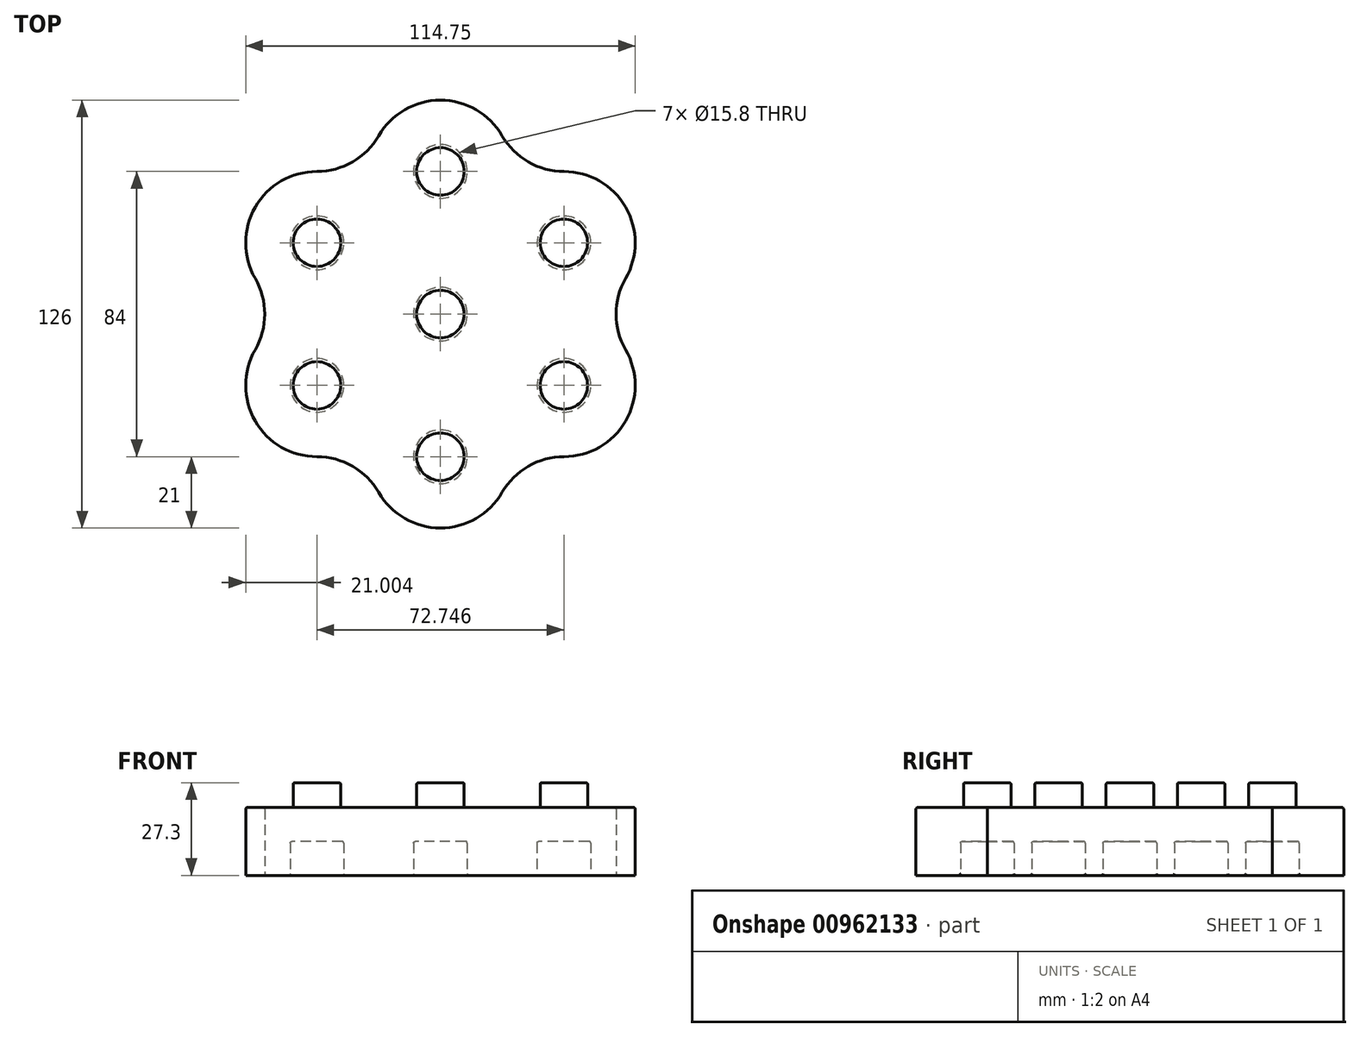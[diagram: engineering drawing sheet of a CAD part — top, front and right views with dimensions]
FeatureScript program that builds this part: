
annotation { "Feature Type Name" : "Feature", "Feature Type Description" : "" }
export const myFeature = defineFeature(function(context is Context, id is Id, definition is map)
    precondition{}
    {
        {
            assignVariable(context, id + "F0", {"name" : "inner_circle_extrude", "anyValue" : 10});
        }
        {
            assignVariable(context, id + "F1", {"name" : "nipple_circle_extrude", "anyValue" : 7.3});
        }
        {
            assignVariable(context, id + "F2", {"name" : "outer_circle_extrude", "anyValue" : 20});
        }
        {
            assignVariable(context, id + "F3", {"name" : "fillet", "anyValue" : 0.5});
        }
        {
            var Q0;
            Q0=qCreatedBy(makeId("Top.planeOp"),FACE);
            var sketch = newSketch(context, id + "F4", { "sketchPlane" : qUnion([Q0])});
            skCircle(sketch, "E0", {"center": v(0, 42) * mm, "radius": 7.9 * mm});
            skCircle(sketch, "E1", {"center": v(0, 0) * mm, "radius": 7.9 * mm});
            skArc(sketch, "E2.converted", {"start": v(18.19, 31.5) * mm, "mid": v(18.19, 52.5) * mm, "end": v(0, 63) * mm});
            skArc(sketch, "E3.converted", {"start": v(-18.19, 10.5) * mm, "mid": v(-18.54, 9.87) * mm, "end": v(-18.87, 9.22) * mm});
            skPoint(sketch, "E4.orphan", {"position": v(-18.87, 9.22) * mm});
            skArc(sketch, "E5.MirrorC", {"start": v(18.19, 10.5) * mm, "mid": v(15.37, 21) * mm, "end": v(18.19, 31.5) * mm});
            skArc(sketch, "E6.converted", {"start": v(-54.56, 10.5) * mm, "mid": v(-46.87, 2.81) * mm, "end": v(-36.37, 0) * mm});
            skArc(sketch, "E7.trimOffspring", {"start": v(0, -21) * mm, "mid": v(18.19, -10.5) * mm, "end": v(18.19, 10.5) * mm});
            skCircle(sketch, "E8", {"center": v(-36.37, 21) * mm, "radius": 7.9 * mm});
            skArc(sketch, "E9.converted", {"start": v(-18.19, 73.5) * mm, "mid": v(-36.37, 84) * mm, "end": v(-54.56, 73.5) * mm});
            skArc(sketch, "E10", {"start": v(-18.19, 73.5) * mm, "mid": v(-10.5, 65.81) * mm, "end": v(0, 63) * mm});
            skCircle(sketch, "E11", {"center": v(-36.37, 63) * mm, "radius": 7.9 * mm});
            skArc(sketch, "E12.converted", {"start": v(-72.75, 63) * mm, "mid": v(-90.93, 52.5) * mm, "end": v(-90.93, 31.5) * mm});
            skArc(sketch, "E13.converted", {"start": v(-54.56, -31.5) * mm, "mid": v(-36.37, -42) * mm, "end": v(-18.19, -31.5) * mm});
            skArc(sketch, "E14", {"start": v(-90.93, 10.5) * mm, "mid": v(-90.93, -10.5) * mm, "end": v(-72.75, -21) * mm});
            skArc(sketch, "E15", {"start": v(-72.75, 63) * mm, "mid": v(-62.25, 65.81) * mm, "end": v(-54.56, 73.5) * mm});
            skArc(sketch, "E16", {"start": v(0, -21) * mm, "mid": v(-10.5, -23.81) * mm, "end": v(-18.19, -31.5) * mm});
            skArc(sketch, "E17", {"start": v(-54.56, -31.5) * mm, "mid": v(-62.25, -23.81) * mm, "end": v(-72.75, -21) * mm});
            skArc(sketch, "E18", {"start": v(-90.93, 10.5) * mm, "mid": v(-88.12, 21) * mm, "end": v(-90.93, 31.5) * mm});
            skCircle(sketch, "E19", {"center": v(-72.75, 42) * mm, "radius": 7.9 * mm});
            skCircle(sketch, "E20", {"center": v(-72.75, 0) * mm, "radius": 7.9 * mm});
            skCircle(sketch, "E21", {"center": v(-36.37, -21) * mm, "radius": 7.9 * mm});
            skSolve(sketch);
        }
        {
            var Q0;
            Q0=makeQuery(id+"F4.imprint","IMPRINT",FACE,{"disambiguationData":[TD([[makeQuery(id+"F4.imprint","IMPRINT",EDGE,{"derivedFrom":sQuery(id+"F4.wireOp",EDGE,"ScaTM9CG-l0WX-AUfX-dH3G-diZ5i2Zft3Bz")}),1.0]])]});
            var Q1;
            Q1=makeQuery(id+"F4.imprint","IMPRINT",FACE,{"disambiguationData":[TD([[makeQuery(id+"F4.imprint","IMPRINT",EDGE,{"derivedFrom":sQuery(id+"F4.wireOp",EDGE,"E0")}),1.0]])]});
            var Q2;
            Q2=makeQuery(id+"F4.imprint","IMPRINT",FACE,{"disambiguationData":[TD([[makeQuery(id+"F4.imprint","IMPRINT",EDGE,{"derivedFrom":sQuery(id+"F4.wireOp",EDGE,"E1")}),1.0]])]});
            var Q3;
            Q3=makeQuery(id+"F4.imprint","IMPRINT",FACE,{"disambiguationData":[TD([[makeQuery(id+"F4.imprint","IMPRINT",EDGE,{"derivedFrom":sQuery(id+"F4.wireOp",EDGE,"E8")}),1.0]])]});
            var Q4;
            Q4=makeQuery(id+"F4.imprint","IMPRINT",FACE,{"disambiguationData":[TD([[makeQuery(id+"F4.imprint","IMPRINT",EDGE,{"derivedFrom":sQuery(id+"F4.wireOp",EDGE,"E11")}),1.0]])]});
            var Q5;
            Q5=makeQuery(id+"F4.imprint","IMPRINT",FACE,{"disambiguationData":[TD([[makeQuery(id+"F4.imprint","IMPRINT",EDGE,{"derivedFrom":sQuery(id+"F4.wireOp",EDGE,"E0")}),-1.0]])]});
            var Q6;
            Q6=makeQuery(id+"F4.imprint","IMPRINT",FACE,{"disambiguationData":[TD([[makeQuery(id+"F4.imprint","IMPRINT",EDGE,{"derivedFrom":sQuery(id+"F4.wireOp",EDGE,"E19")}),1.0]])]});
            var Q7;
            Q7=makeQuery(id+"F4.imprint","IMPRINT",FACE,{"disambiguationData":[TD([[makeQuery(id+"F4.imprint","IMPRINT",EDGE,{"derivedFrom":sQuery(id+"F4.wireOp",EDGE,"E20")}),1.0]])]});
            var Q8;
            Q8=makeQuery(id+"F4.imprint","IMPRINT",FACE,{"disambiguationData":[TD([[makeQuery(id+"F4.imprint","IMPRINT",EDGE,{"derivedFrom":sQuery(id+"F4.wireOp",EDGE,"E21")}),1.0]])]});
            extrude(context, id + "F5", {"entities" : qUnion([Q0, Q1, Q2, Q3, Q4, Q5, Q6, Q7, Q8]), "depth" : (getVariable(context, 'outer_circle_extrude')) * mm, "offsetDistance" : 25 * mm});
        }
        {
            var Q0;
            Q0=makeQuery(id+"F4.imprint","IMPRINT",FACE,{"disambiguationData":[TD([[makeQuery(id+"F4.imprint","IMPRINT",EDGE,{"derivedFrom":sQuery(id+"F4.wireOp",EDGE,"E0")}),1.0]])]});
            var Q1;
            Q1=makeQuery(id+"F4.imprint","IMPRINT",FACE,{"disambiguationData":[TD([[makeQuery(id+"F4.imprint","IMPRINT",EDGE,{"derivedFrom":sQuery(id+"F4.wireOp",EDGE,"E1")}),1.0]])]});
            var Q2;
            Q2=makeQuery(id+"F4.imprint","IMPRINT",FACE,{"disambiguationData":[TD([[makeQuery(id+"F4.imprint","IMPRINT",EDGE,{"derivedFrom":sQuery(id+"F4.wireOp",EDGE,"E8")}),1.0]])]});
            var Q3;
            Q3=makeQuery(id+"F4.imprint","IMPRINT",FACE,{"disambiguationData":[TD([[makeQuery(id+"F4.imprint","IMPRINT",EDGE,{"derivedFrom":sQuery(id+"F4.wireOp",EDGE,"E11")}),1.0]])]});
            var Q4;
            Q4=makeQuery(id+"F4.imprint","IMPRINT",FACE,{"disambiguationData":[TD([[makeQuery(id+"F4.imprint","IMPRINT",EDGE,{"derivedFrom":sQuery(id+"F4.wireOp",EDGE,"E19")}),1.0]])]});
            var Q5;
            Q5=makeQuery(id+"F4.imprint","IMPRINT",FACE,{"disambiguationData":[TD([[makeQuery(id+"F4.imprint","IMPRINT",EDGE,{"derivedFrom":sQuery(id+"F4.wireOp",EDGE,"E20")}),1.0]])]});
            var Q6;
            Q6=makeQuery(id+"F4.imprint","IMPRINT",FACE,{"disambiguationData":[TD([[makeQuery(id+"F4.imprint","IMPRINT",EDGE,{"derivedFrom":sQuery(id+"F4.wireOp",EDGE,"E21")}),1.0]])]});
            extrude(context, id + "F6", {"entities" : qUnion([Q0, Q1, Q2, Q3, Q4, Q5, Q6]), "operationType" : NewBodyOperationType.REMOVE, "depth" : (getVariable(context, 'inner_circle_extrude')) * mm, "offsetDistance" : 25 * mm});
        }
        {
            var Q0;
            Q0=makeQuery(id+"F5.opExtrude","CAP_FACE",FACE,{"disambiguationData":[OSD([sQuery(id+"F4.wireOp",EDGE,"E2.converted"),sQuery(id+"F4.wireOp",EDGE,"E3.converted"),sQuery(id+"F4.wireOp",EDGE,"MIaug4t6-5uLj-SX17-JixO-nkbqJCue0yvX"),sQuery(id+"F4.wireOp",EDGE,"E5.MirrorC")])],"isStart":false});
            var sketch = newSketch(context, id + "F7", { "sketchPlane" : qUnion([Q0])});
            skCircle(sketch, "E22", {"center": v(0, 0) * mm, "radius": 7 * mm});
            skCircle(sketch, "E23", {"center": v(0, 42) * mm, "radius": 7 * mm});
            skCircle(sketch, "E24", {"center": v(-36.37, 21) * mm, "radius": 7 * mm});
            skCircle(sketch, "E25", {"center": v(-36.37, 63) * mm, "radius": 7 * mm});
            skCircle(sketch, "E26", {"center": v(-72.75, 42) * mm, "radius": 7 * mm});
            skCircle(sketch, "E27", {"center": v(-72.75, 0) * mm, "radius": 7 * mm});
            skCircle(sketch, "E28", {"center": v(-36.37, -21) * mm, "radius": 7 * mm});
            skSolve(sketch);
        }
        {
            var Q0;
            Q0=makeQuery(id+"F7.imprint","IMPRINT",FACE,{"disambiguationData":[TD([[makeQuery(id+"F7.imprint","IMPRINT",EDGE,{"derivedFrom":sQuery(id+"F7.wireOp",EDGE,"E22")}),1.0]])]});
            var Q1;
            Q1=makeQuery(id+"F7.imprint","IMPRINT",FACE,{"disambiguationData":[TD([[makeQuery(id+"F7.imprint","IMPRINT",EDGE,{"derivedFrom":sQuery(id+"F7.wireOp",EDGE,"Dg55u7MG-Wcnn-qXMQ-j3jR-78wnB7IFwmOc")}),1.0]])]});
            var Q2;
            Q2=makeQuery(id+"F7.imprint","IMPRINT",FACE,{"disambiguationData":[TD([[makeQuery(id+"F7.imprint","IMPRINT",EDGE,{"derivedFrom":sQuery(id+"F7.wireOp",EDGE,"E23")}),1.0]])]});
            var Q3;
            Q3=makeQuery(id+"F7.imprint","IMPRINT",FACE,{"disambiguationData":[TD([[makeQuery(id+"F7.imprint","IMPRINT",EDGE,{"derivedFrom":sQuery(id+"F7.wireOp",EDGE,"E24")}),1.0]])]});
            var Q4;
            Q4=makeQuery(id+"F7.imprint","IMPRINT",FACE,{"disambiguationData":[TD([[makeQuery(id+"F7.imprint","IMPRINT",EDGE,{"derivedFrom":sQuery(id+"F7.wireOp",EDGE,"E25")}),1.0]])]});
            var Q5;
            Q5=makeQuery(id+"F7.imprint","IMPRINT",FACE,{"disambiguationData":[TD([[makeQuery(id+"F7.imprint","IMPRINT",EDGE,{"derivedFrom":sQuery(id+"F7.wireOp",EDGE,"E28")}),1.0]])]});
            var Q6;
            Q6=makeQuery(id+"F7.imprint","IMPRINT",FACE,{"disambiguationData":[TD([[makeQuery(id+"F7.imprint","IMPRINT",EDGE,{"derivedFrom":sQuery(id+"F7.wireOp",EDGE,"E27")}),1.0]])]});
            var Q7;
            Q7=makeQuery(id+"F7.imprint","IMPRINT",FACE,{"disambiguationData":[TD([[makeQuery(id+"F7.imprint","IMPRINT",EDGE,{"derivedFrom":sQuery(id+"F7.wireOp",EDGE,"E26")}),1.0]])]});
            extrude(context, id + "F8", {"entities" : qUnion([Q0, Q1, Q2, Q3, Q4, Q5, Q6, Q7]), "operationType" : NewBodyOperationType.ADD, "depth" : (getVariable(context, 'nipple_circle_extrude')) * mm, "offsetDistance" : 25 * mm});
        }
        {
            var Q0;
            Q0=makeQuery(id+"F8.opExtrude","CAP_EDGE",EDGE,{"disambiguationData":[OSD([sQuery(id+"F7.wireOp",EDGE,"E22")])],"isStart":false});
            var Q1;
            Q1=makeQuery(id+"F5.opExtrude","CAP_EDGE",EDGE,{"disambiguationData":[OSD([sQuery(id+"F4.wireOp",EDGE,"ScaTM9CG-l0WX-AUfX-dH3G-diZ5i2Zft3Bz")])],"isStart":false});
            var Q2;
            Q2=makeQuery(id+"F5.opExtrude","CAP_EDGE",EDGE,{"disambiguationData":[OSD([sQuery(id+"F4.wireOp",EDGE,"ScaTM9CG-l0WX-AUfX-dH3G-diZ5i2Zft3Bz")])],"isStart":true});
            var Q3;
            Q3=makeQuery(id+"F6.boolean.opBoolean","COPY",EDGE,{"derivedFrom":makeQuery(id+"F6.opExtrude","CAP_EDGE",EDGE,{"disambiguationData":[OSD([sQuery(id+"F4.wireOp",EDGE,"E0")])],"isStart":true})});
            var Q4;
            Q4=makeQuery(id+"F6.boolean.opBoolean","COPY",FACE,{"derivedFrom":makeQuery(id+"F6.opExtrude","CAP_FACE",FACE,{"disambiguationData":[OSD([sQuery(id+"F4.wireOp",EDGE,"E0")])],"isStart":false})});
            var Q5;
            Q5=makeQuery(id+"F6.boolean.opBoolean","COPY",EDGE,{"derivedFrom":makeQuery(id+"F6.opExtrude","CAP_EDGE",EDGE,{"disambiguationData":[OSD([sQuery(id+"F4.wireOp",EDGE,"E1")])],"isStart":true})});
            var Q6;
            Q6=makeQuery(id+"F6.boolean.opBoolean","COPY",EDGE,{"derivedFrom":makeQuery(id+"F6.opExtrude","CAP_EDGE",EDGE,{"disambiguationData":[OSD([sQuery(id+"F4.wireOp",EDGE,"E1")])],"isStart":false})});
            var Q7;
            Q7=makeQuery(id+"F8.opExtrude","CAP_EDGE",EDGE,{"disambiguationData":[OSD([sQuery(id+"F7.wireOp",EDGE,"Dg55u7MG-Wcnn-qXMQ-j3jR-78wnB7IFwmOc")])],"isStart":true});
            var Q8;
            Q8=makeQuery(id+"F8.opExtrude","CAP_EDGE",EDGE,{"disambiguationData":[OSD([sQuery(id+"F7.wireOp",EDGE,"Dg55u7MG-Wcnn-qXMQ-j3jR-78wnB7IFwmOc")])],"isStart":false});
            var Q9;
            Q9=makeQuery(id+"F8.opExtrude","CAP_EDGE",EDGE,{"disambiguationData":[OSD([sQuery(id+"F7.wireOp",EDGE,"E23")])],"isStart":false});
            var Q10;
            Q10=makeQuery(id+"F8.opExtrude","CAP_EDGE",EDGE,{"disambiguationData":[OSD([sQuery(id+"F7.wireOp",EDGE,"E23")])],"isStart":true});
            var Q11;
            Q11=makeQuery(id+"F5.opExtrude","CAP_EDGE",EDGE,{"disambiguationData":[OSD([sQuery(id+"F4.wireOp",EDGE,"E2.converted")])],"isStart":false});
            var Q12;
            Q12=makeQuery(id+"F8.opExtrude","CAP_EDGE",EDGE,{"disambiguationData":[OSD([sQuery(id+"F7.wireOp",EDGE,"E24")])],"isStart":true});
            var Q13;
            Q13=makeQuery(id+"F8.opExtrude","CAP_EDGE",EDGE,{"disambiguationData":[OSD([sQuery(id+"F7.wireOp",EDGE,"E24")])],"isStart":false});
            var Q14;
            Q14=makeQuery(id+"F6.boolean.opBoolean","COPY",FACE,{"derivedFrom":makeQuery(id+"F6.opExtrude","SWEPT_FACE",FACE,{"disambiguationData":[OSD([sQuery(id+"F4.wireOp",EDGE,"E8")])]})});
            var Q15;
            Q15=makeQuery(id+"F8.opExtrude","SWEPT_FACE",FACE,{"disambiguationData":[OSD([sQuery(id+"F7.wireOp",EDGE,"E25")])]});
            var Q16;
            Q16=makeQuery(id+"F6.boolean.opBoolean","COPY",FACE,{"derivedFrom":makeQuery(id+"F6.opExtrude","SWEPT_FACE",FACE,{"disambiguationData":[OSD([sQuery(id+"F4.wireOp",EDGE,"E11")])]})});
            var Q17;
            Q17=makeQuery(id+"F8.opExtrude","SWEPT_FACE",FACE,{"disambiguationData":[OSD([sQuery(id+"F7.wireOp",EDGE,"E27")])]});
            var Q18;
            Q18=makeQuery(id+"F8.opExtrude","SWEPT_FACE",FACE,{"disambiguationData":[OSD([sQuery(id+"F7.wireOp",EDGE,"E28")])]});
            var Q19;
            Q19=makeQuery(id+"F8.opExtrude","SWEPT_FACE",FACE,{"disambiguationData":[OSD([sQuery(id+"F7.wireOp",EDGE,"E26")])]});
            var Q20;
            Q20=makeQuery(id+"F6.boolean.opBoolean","COPY",FACE,{"derivedFrom":makeQuery(id+"F6.opExtrude","SWEPT_FACE",FACE,{"disambiguationData":[OSD([sQuery(id+"F4.wireOp",EDGE,"E19")])]})});
            var Q21;
            Q21=makeQuery(id+"F6.boolean.opBoolean","COPY",FACE,{"derivedFrom":makeQuery(id+"F6.opExtrude","SWEPT_FACE",FACE,{"disambiguationData":[OSD([sQuery(id+"F4.wireOp",EDGE,"E20")])]})});
            var Q22;
            Q22=makeQuery(id+"F6.boolean.opBoolean","COPY",FACE,{"derivedFrom":makeQuery(id+"F6.opExtrude","SWEPT_FACE",FACE,{"disambiguationData":[OSD([sQuery(id+"F4.wireOp",EDGE,"E21")])]})});
            var Q23;
            Q23=makeQuery(id+"F8.opExtrude","CAP_EDGE",EDGE,{"disambiguationData":[OSD([sQuery(id+"F7.wireOp",EDGE,"E22")])],"isStart":true});
            fillet(context, id + "F9", {"entities" : qUnion([Q0, Q1, Q2, Q3, Q4, Q5, Q6, Q7, Q8, Q9, Q10, Q11, Q12, Q13, Q14, Q15, Q16, Q17, Q18, Q19, Q20, Q21, Q22, Q23]), "radius" : (getVariable(context, 'fillet')) * mm, "tangentPropagation" : true, "allowEdgeOverflow" : false});
        }
    });
